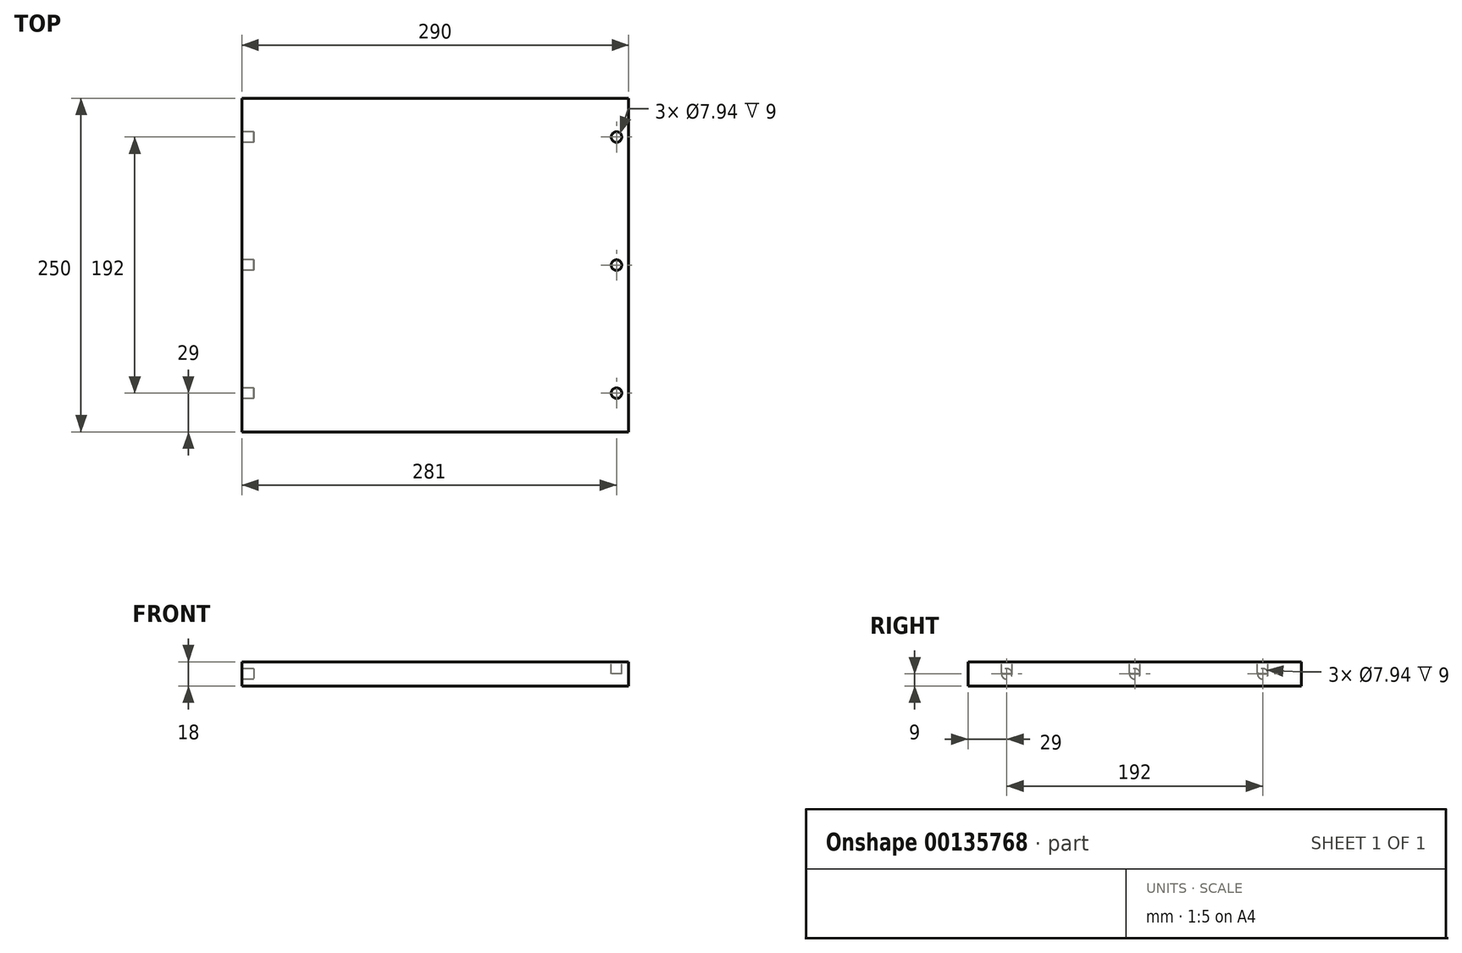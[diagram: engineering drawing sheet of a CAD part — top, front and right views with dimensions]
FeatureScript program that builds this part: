
annotation { "Feature Type Name" : "Feature", "Feature Type Description" : "" }
export const myFeature = defineFeature(function(context is Context, id is Id, definition is map)
    precondition{}
    {
        {
            var Q0;
            Q0=qCreatedBy(makeId("Top.planeOp"),FACE);
            var sketch = newSketch(context, id + "F0", { "sketchPlane" : qUnion([Q0])});
            skLineSegment(sketch, "E0.bottom", {"start": v(145, -125) * mm, "end": v(-145, -125) * mm});
            skLineSegment(sketch, "E0.top", {"start": v(145, 125) * mm, "end": v(-145, 125) * mm});
            skLineSegment(sketch, "E0.left", {"start": v(145, -125) * mm, "end": v(145, 125) * mm});
            skLineSegment(sketch, "E0.right", {"start": v(-145, -125) * mm, "end": v(-145, 125) * mm});
            skPoint(sketch, "E0.middle", {"position": v(0, 0) * mm});
            skSolve(sketch);
        }
        {
            var Q0;
            Q0 = qSketchRegion(id + "F0", true);
            extrude(context, id + "F1", {"entities" : qUnion([Q0]), "endBound" : BoundingType.SYMMETRIC, "depth" : 18 * mm});
        }
        {
            var Q0;
            Q0=makeQuery(id+"F1.opExtrude","CAP_FACE",FACE,{"disambiguationData":[OSD([sQuery(id+"F0.wireOp",EDGE,"E0.bottom"),sQuery(id+"F0.wireOp",EDGE,"E0.top"),sQuery(id+"F0.wireOp",EDGE,"E0.left"),sQuery(id+"F0.wireOp",EDGE,"E0.right")])],"isStart":false});
            var sketch = newSketch(context, id + "F2", { "sketchPlane" : qUnion([Q0])});
            skCircle(sketch, "E1", {"center": v(136, 0) * mm, "radius": 3.97 * mm});
            skCircle(sketch, "E2", {"center": v(136, 96) * mm, "radius": 3.97 * mm});
            skCircle(sketch, "E3.MirrorC", {"center": v(136, -96) * mm, "radius": 3.97 * mm});
            skSolve(sketch);
        }
        {
            var Q0;
            Q0 = qSketchRegion(id + "F2", true);
            extrude(context, id + "F3", {"entities" : qUnion([Q0]), "operationType" : NewBodyOperationType.REMOVE, "oppositeDirection" : true, "depth" : 9 * mm});
        }
        {
            var Q0;
            Q0=makeQuery(id+"F1.opExtrude","SWEPT_FACE",FACE,{"disambiguationData":[OSD([sQuery(id+"F0.wireOp",EDGE,"E0.right")])]});
            var sketch = newSketch(context, id + "F4", { "sketchPlane" : qUnion([Q0])});
            skCircle(sketch, "E4", {"center": v(0, 0) * mm, "radius": 3.97 * mm});
            skPoint(sketch, "E4.centerSnap0", {"position": v(0, -9) * mm});
            skCircle(sketch, "E5", {"center": v(96, 0) * mm, "radius": 3.97 * mm});
            skCircle(sketch, "E6.MirrorC", {"center": v(-96, 0) * mm, "radius": 3.97 * mm});
            skSolve(sketch);
        }
        {
            var Q0;
            Q0 = qSketchRegion(id + "F4", true);
            extrude(context, id + "F5", {"entities" : qUnion([Q0]), "operationType" : NewBodyOperationType.REMOVE, "oppositeDirection" : true, "depth" : 9 * mm});
        }
    });
